# Revit family: FORM-20-REC-CM_no_ESC_Lens_Lighting_Non-Hosted_R20
name_source: partatom
category: Lighting Fixtures
units: mm (PartAtom-declared; Revit-internal decimal feet)

## family parameters
Always vertical = Yes
Cut with Voids When Loaded = No
Light Source = Yes
OmniClass Number = 23.80.70.00
OmniClass Title = Lighting
Part Type = Normal
Room Calculation Point = No
Round Connector Dimension = Use Diameter
Shared = No
Work Plane-Based = No

## types (24) — shared parameters
Applicable Standards = BS EN 55015, BS EN 61547, BS EN 61000-3-2, BS EN 61000-3-3, ETSI EN 301 489-1, ETSI EN 301 489-17, BS EN 1838, BS EN ISO 7010, BS EN 62471, BS EN 60598-2-22
Charging Method = Intelligent Current Limited Constant Voltage
Color Filter = 16777215
Diffuser = Polycarbonate
Dimensions (L x W x H) = 220 x 18 x 110
Dimming Lamp Color Temperature Shift = <None>
Earth Leakage = 0.35
Emit Shape Visible in Rendering = No
IK Rating = IK03
IP Rating = IP20
Inrush Current (Max) = 10A<144µs
Lamp = 18 x LED, 170,000 hours
Manufacturer = Clevertronics
Mounting = Recessed Ceiling Mount, Double Sided
Operating Mode = Maintained
Operating Temperature = 0 ºC - 40ºC
Operating Voltage = 220-240V~ 50Hz
Photometric Web File = generic
Power Factor = 0.28 (Standby, Maintained), 0.42 (Max)
Tilt Angle = 90.00°
zero-valued in all types: Default Elevation

## per-type parameters (varying)
| type | Battery | Battery Type | Construction | Description | MIC Number | Power Consumption | Power Consumption (Standby - Lamp Off) | Replacement Battery | Replacement Emergency Driver | Replacement Item | Supply Current | Testing System | Type Comments | Weight |
| FORM-20-REC-CM-CS-L10 | 3.3V 2500mAh | Lithium Nanophosphate | PCM Box with PC/Aluminium Extrusion Blade | Form 20m Exit, Recessed Ceiling Mount, Cable Suspended, L10 Nanophosphate, Clevertest Plus, Picto All, Double Sided, Brushed Aluminium Frame | UKA01310150001 | 3.3W | 1.2W | 1530050 | UKM01370300001 LLEDDRV2CH-RR-2C170-6C30-15-CKIT |  | 18.61 (Standby, Maintained), 34.30 (Max) - (mA) | Clevertest Plus Enabled (Not Activated By Default) | Form 20M Exit, Rec CM CS, L10, CTP, Alm | 0.65kg |
| FORM-20-REC-CM-CS-L10-DALI | 3.3V 2500mAh | Lithium Nanophosphate | PCM Box with PC/Aluminium Extrusion Blade | Form 20m Exit, Recessed Ceiling Mount, Cable Suspended, L10 Nanophosphate, DALI Emergency, Picto All, Double Sided, Brushed Aluminium Frame | UKA01210240002 | 3.6W | 1.5W | 1530050 | UKM01270080002 LLEDDRV2CH-RR-2C170-6C30-15-CKIT-DALI | 8003068 | 19.91 (Standby, Maintained), 35.60 (Max) - (mA) | DALI Registered | Form 20M Exit, Rec CM CS, L10, Dali Reg, Alm | 0.65kg |
| FORM-20-REC-CM-CS-L10-HVG | 3.3V 2500mAh | Lithium Nanophosphate | PCM Box with PC/Aluminium Extrusion Blade | Form 20m Exit, Recessed Ceiling Mount, Cable Suspended, L10 Nanophosphate, Zoneworks XT Hive, Picto All, Double Sided, Brushed Aluminium Frame | UKA01810300001 | 3.6W | 1.5W | 1530050 | UKM01870370001 LLEDDRV2CH-RR-2C170-6C30-15-CKIT-HVGEXTA | 8003345 | 19.91 (Standby, Maintained), 35.60 (Max) - (mA) | Zoneworks XT HIVE (RF) | Form 20M Exit, Rec CM CS, L10, ZW HT Hive, Alm | 0.65kg |
| FORM-20-REC-CM-CS-LP | 3.2V 1100mAh | Lithium Iron Phosphate | PCM Box with PC/Aluminium Extrusion Blade | Form 20m Exit, Recessed Ceiling Mount, Cable Suspended, CLP, Clevertest Plus, Picto All, Double Sided, Brushed Aluminium Frame | UKA02310230001 | 3.3W | 1.2W | 1550150 | UKM02370210001 CLEDDRV2CH-RR-2C170-6C30-15-CKIT |  | 18.61 (Standby, Maintained), 34.30 (Max) - (mA) | Clevertest Plus Enabled (Not Activated By Default) | Form 20M Exit, Rec CM CS, CLP, CTP, Alm | 0.65kg |
| FORM-20-REC-CM-CS-LP-DALI | 3.2V 1100mAh | Lithium Iron Phosphate | PCM Box with PC/Aluminium Extrusion Blade | Form 20m Exit, Recessed Ceiling Mount, Cable Suspended, CLP, DALI Emergency, Picto All, Double Sided, Brushed Aluminium Frame | UKA02210240002 | 3.6W | 1.5W | 1550150 | UKM02270080002 CLEDDRV2CH-RR-2C170-6C30-15-CKIT-DALI | 8003068 | 19.91 (Standby, Maintained), 35.60 (Max) - (mA) | DALI Registered | Form 20M Exit, Rec CM CS, CLP, Dali Reg, Alm | 0.65kg |
| FORM-20-REC-CM-CS-LP-HVG | 3.2V 1100mAh | Lithium Iron Phosphate | PCM Box with PC/Aluminium Extrusion Blade | Form 20m Exit, Recessed Ceiling Mount, Cable Suspended, CLP, Zoneworks XT Hive, Picto All, Double Sided, Brushed Aluminium Frame | UKA02810230001 | 3.6W | 1.5W | 1550150 | UKM02870300001 CLEDDRV2CH-RR-2C170-6C30-15-CKIT-HVGEXTA | 8003345 | 19.91 (Standby, Maintained), 35.60 (Max) - (mA) | Zoneworks XT HIVE (RF) | Form 20M Exit, Rec CM CS, CLP, ZW HT Hive, Alm | 0.65kg |
| FORM-20-REC-CM-CS-REM-L10 | 3.3V 2500mAh | Lithium Nanophosphate | PC/Aluminium Extrusion Blade, with remote hardware | Form 20m Exit, Recessed Ceiling Mount, Cable Suspended, Remote Gear, L10 Nanophosphate, Clevertest Plus, Picto All, Double Sided, Brushed Aluminium Frame | UKA01310240001 | 3.3W | 1.2W | 1530050 | UKM01370300001 LLEDDRV2CH-RR-2C170-6C30-15-CKIT |  | 18.61 (Standby, Maintained), 34.30 (Max) - (mA) | Clevertest Plus Enabled (Not Activated By Default) |  | 0.55kg |
| FORM-20-REC-CM-CS-REM-L10-DALI | 3.3V 2500mAh | Lithium Nanophosphate | PC/Aluminium Extrusion Blade, with remote hardware | Form 20m Exit, Recessed Ceiling Mount, Cable Suspended, Remote Gear, L10 Nanophosphate, DALI Emergency, Picto All, Double Sided, Brushed Aluminium Frame | UKA01210220002 | 3.6W | 1.5W | 1530050 | UKM01270080002 LLEDDRV2CH-RR-2C170-6C30-15-CKIT-DALI | 8003068 | 19.91 (Standby, Maintained), 35.60 (Max) - (mA) | DALI Registered | Form 20M Exit, Rec CM CS, REM, L10, Dali Reg, Alm | 0.55kg |
| FORM-20-REC-CM-CS-REM-L10-HVG | 3.3V 2500mAh | Lithium Nanophosphate | PC/Aluminium Extrusion Blade, with remote hardware | Form 20m Exit, Recessed Ceiling Mount, Cable Suspended, Remote Gear, L10 Nanophosphate, Zoneworks XT Hive, Picto All, Double Sided, Brushed Aluminium Frame | UKA01810280001 | 3.6W | 1.5W | 1530050 | UKM01870300001 LLEDDRV2CH-RR-2C170-6C30-15-CKIT-HVG | 8003335 | 19.91 (Standby, Maintained), 35.60 (Max) - (mA) | Zoneworks XT HIVE (RF) |  | 0.55kg |
| FORM-20-REC-CM-CS-REM-LP | 3.2V 1100mAh | Lithium Iron Phosphate | PC/Aluminium Extrusion Blade, with remote hardware | Form 20m Exit, Recessed Ceiling Mount, Cable Suspended, Remote Gear, CLP, Clevertest Plus, Picto All, Double Sided, Brushed Aluminium Frame | UKA02310210001 | 3.3W | 1.2W | 1550150 | UKM02370210001 CLEDDRV2CH-RR-2C170-6C30-15-CKIT |  | 18.61 (Standby, Maintained), 34.30 (Max) - (mA) | Clevertest Plus Enabled (Not Activated By Default) | Form 20M Exit, Rec CM CS, REM, CLP, CTP, Alm | 0.55kg |
| FORM-20-REC-CM-CS-REM-LP-DALI | 3.2V 1100mAh | Lithium Iron Phosphate | PC/Aluminium Extrusion Blade, with remote hardware | Form 20m Exit, Recessed Ceiling Mount, Cable Suspended, Remote Gear, CLP, DALI Emergency, Picto All, Double Sided, Brushed Aluminium Frame | UKA02210220002 | 3.6W | 1.5W | 1550150 | UKM02270080002 CLEDDRV2CH-RR-2C170-6C30-15-CKIT-DALI | 8003068 | 19.91 (Standby, Maintained), 35.60 (Max) - (mA) | DALI Registered |  | 0.55kg |
| FORM-20-REC-CM-CS-REM-LP-HVG | 3.2V 1100mAh | Lithium Iron Phosphate | PC/Aluminium Extrusion Blade, with remote hardware | Form 20m Exit, Recessed Ceiling Mount, Cable Suspended, Remote Gear, CLP, Zoneworks XT Hive, Picto All, Double Sided, Brushed Aluminium Frame | UKA02810210001 | 3.6W | 1.5W | 1550150 | UKM02870260001 CLEDDRV2CH-RR-2C170-6C30-15-CKIT-HVG | 8003335 | 19.91 (Standby, Maintained), 35.60 (Max) - (mA) | Zoneworks XT HIVE (RF) |  | 0.55kg |
| FORM-20-REC-CM-L10 | 3.3V 2500mAh | Lithium Nanophosphate | PCM Box with PC/Aluminium Extrusion Blade | Form 20m Exit, Recessed Ceiling Mount, L10 Nanophosphate, Clevertest Plus, Picto All, Double Sided, Brushed Aluminium Frame | UKA01310130001 | 3.3W | 1.2W | 1530050 | UKM01370300001 LLEDDRV2CH-RR-2C170-6C30-15-CKIT |  | 18.61 (Standby, Maintained), 34.30 (Max) - (mA) | Clevertest Plus | Form 20M Exit, Rec CM, L10, CTP, Alm | 0.70kg |
| FORM-20-REC-CM-L10-DALI | 3.3V 2500mAh | Lithium Nanophosphate | PCM Box with PC/Aluminium Extrusion Blade | Form 20m Exit, Recessed Ceiling Mount, L10 Nanophosphate, DALI Emergency, Picto All, Double Sided, Brushed Aluminium Frame | UKA01210260002 | 3.6W | 1.5W | 1530050 | UKM01270080002 LLEDDRV2CH-RR-2C170-6C30-15-CKIT-DALI | 8003068 | 19.91 (Standby, Maintained), 35.60 (Max) - (mA) | DALI Registered | Form 20M Exit, Rec CM, L10, Dali Reg, Alm | 0.70kg |
| FORM-20-REC-CM-L10-HVG | 3.3V 2500mAh | Lithium Nanophosphate | PCM Box with PC/Aluminium Extrusion Blade | Form 20m Exit, Recessed Ceiling Mount, L10 Nanophosphate, Zoneworks XT Hive, Picto All, Double Sided, Brushed Aluminium Frame | UKA01810190001 | 3.6W | 1.5W | 1530050 | UKM01870370001 LLEDDRV2CH-RR-2C170-6C30-15-CKIT-HVGEXTA | 8003345 | 19.91 (Standby, Maintained), 35.60 (Max) - (mA) | Zoneworks XT HIVE (RF) | Form 20M Exit, Rec CM, L10, ZW HT Hive, Alm | 0.70kg |
| FORM-20-REC-CM-LP | 3.2V 1100mAh | Lithium Iron Phosphate | PCM Box with PC/Aluminium Extrusion Blade | Form 20m Exit, Recessed Ceiling Mount, CLP, Clevertest Plus, Picto All, Double Sided, Brushed Aluminium Frame | UKA02310130001 | 3.3W | 1.2W | 1550150 | UKM02370210001 CLEDDRV2CH-RR-2C170-6C30-15-CKIT |  | 18.61 (Standby, Maintained), 34.30 (Max) - (mA) | Clevertest Plus Enabled (Not Activated By Default) | Form 20M Exit, Rec CM, CLP, CTP, Alm | 0.70kg |
| FORM-20-REC-CM-LP-DALI | 3.2V 1100mAh | Lithium Iron Phosphate | PCM Box with PC/Aluminium Extrusion Blade | Form 20m Exit, Recessed Ceiling Mount, CLP, DALI Emergency, Picto All, Double Sided, Brushed Aluminium Frame | UKA02210260002 | 3.6W | 1.5W | 1550150 | UKM02270080002 CLEDDRV2CH-RR-2C170-6C30-15-CKIT-DALI | 8003068 | 19.91 (Standby, Maintained), 35.60 (Max) - (mA) | DALI Registered | Form 20M Exit, Rec CM, CLP, Dali Reg, Alm | 0.70kg |
| FORM-20-REC-CM-LP-HVG | 3.2V 1100mAh | Lithium Iron Phosphate | PCM Box with PC/Aluminium Extrusion Blade | Form 20m Exit, Recessed Ceiling Mount, CLP, Zoneworks XT Hive, Picto All, Double Sided, Brushed Aluminium Frame | UKA02810250001 | 3.6W | 1.5W | 1550150 | UKM02870300001 CLEDDRV2CH-RR-2C170-6C30-15-CKIT-HVGEXTA | 8003345 | 19.91 (Standby, Maintained), 35.60 (Max) - (mA) | Zoneworks XT HIVE (RF) | Form 20M Exit, Rec CM, CLP, ZW HT Hive, Alm | 0.70kg |
| FORM-20-REC-CM-RS-L10 | 3.3V 2500mAh | Lithium Nanophosphate | PCM Box with PC/Aluminium Extrusion Blade | Form 20m Exit, Recessed Ceiling Mount, Rod Suspended, L10 Nanophosphate, Clevertest Plus, Picto All, Double Sided, Brushed Aluminium Frame | UKA01310140001 | 3.3W | 1.2W | 1530050 | UKM01370300001 LLEDDRV2CH-RR-2C170-6C30-15-CKIT |  | 18.61 (Standby, Maintained), 34.30 (Max) - (mA) | Clevertest Plus Enabled (Not Activated By Default) | Form 20M Exit, Rec CM RS, L10, CTP, Alm | 1.20kg |
| FORM-20-REC-CM-RS-L10-DALI | 3.3V 2500mAh | Lithium Nanophosphate | PCM Box with PC/Aluminium Extrusion Blade | Form 20m Exit, Recessed Ceiling Mount, Rod Suspended, L10 Nanophosphate, DALI Emergency, Picto All, Double Sided, Brushed Aluminium Frame | UKA01210250002 | 3.6W | 1.5W | 1530050 | UKM01270080002 LLEDDRV2CH-RR-2C170-6C30-15-CKIT-DALI | 8003068 | 19.91 (Standby, Maintained), 35.60 (Max) - (mA) | DALI Registered | Form 20M Exit, Rec CM RS, L10, Dali Reg, Alm | 1.20kg |
| FORM-20-REC-CM-RS-L10-HVG | 3.3V 2500mAh | Lithium Nanophosphate | PCM Box with PC/Aluminium Extrusion Blade | Form 20m Exit, Recessed Ceiling Mount, Rod Suspended, L10 Nanophosphate, Zoneworks XT Hive, Picto All, Double Sided, Brushed Aluminium Frame | UKA01810200001 | 3.6W | 1.5W | 1530050 | UKM01870370001 LLEDDRV2CH-RR-2C170-6C30-15-CKIT-HVGEXTA | 8003345 | 19.91 (Standby, Maintained), 35.60 (Max) - (mA) | Zoneworks XT HIVE (RF) | Form 20M Exit, Rec CM RS, L10, ZW HT Hive, Alm | 1.20kg |
| FORM-20-REC-CM-RS-LP | 3.2V 1100mAh | Lithium Iron Phosphate | PCM Box with PC/Aluminium Extrusion Blade | Form 20m Exit, Recessed Ceiling Mount, Rod Suspended, CLP, Clevertest Plus, Picto All, Double Sided, Brushed Aluminium Frame | UKA02310240001 | 3.3W | 1.2W | 1550150 | UKM02370210001 CLEDDRV2CH-RR-2C170-6C30-15-CKIT |  | 18.61 (Standby, Maintained), 34.30 (Max) - (mA) | Clevertest Plus Enabled (Not Activated By Default) | Form 20M Exit, Rec CM RS, CLP, CTP, Alm | 1.20kg |
| FORM-20-REC-CM-RS-LP-DALI | 3.2V 1100mAh | Lithium Iron Phosphate | PCM Box with PC/Aluminium Extrusion Blade | Form 20m Exit, Recessed Ceiling Mount, Rod Suspended, CLP, DALI Emergency, Picto All, Double Sided, Brushed Aluminium Frame | UKA02210250002 | 3.6W | 1.5W | 1550150 | UKM02270080002 CLEDDRV2CH-RR-2C170-6C30-15-CKIT-DALI | 8003068 | 19.91 (Standby, Maintained), 35.60 (Max) - (mA) | DALI Registered | Form 20M Exit, Rec CM RS, CLP, Dali Reg, Alm | 1.20kg |
| FORM-20-REC-CM-RS-LP-HVG | 3.2V 1100mAh | Lithium Iron Phosphate | PCM Box with PC/Aluminium Extrusion Blade | Form 20m Exit, Recessed Ceiling Mount, Rod Suspended, CLP, Zoneworks XT Hive, Picto All, Double Sided, Brushed Aluminium Frame | UKA02810240001 | 3.6W | 1.5W | 1550150 | UKM02870300001 CLEDDRV2CH-RR-2C170-6C30-15-CKIT-HVGEXTA | 8003345 | 19.91 (Standby, Maintained), 35.60 (Max) - (mA) | Zoneworks XTHIVE (RF) | Form 20M Exit, Rec CM RS, CLP, ZW HT Hive, Alm | 1.20kg |

note: column(s) folded — value = type name in every type: Model

## geometry (parser evidence)
native form markers: Extrusion x26, Sweep x2
no freeform markers — native parametric forms only
